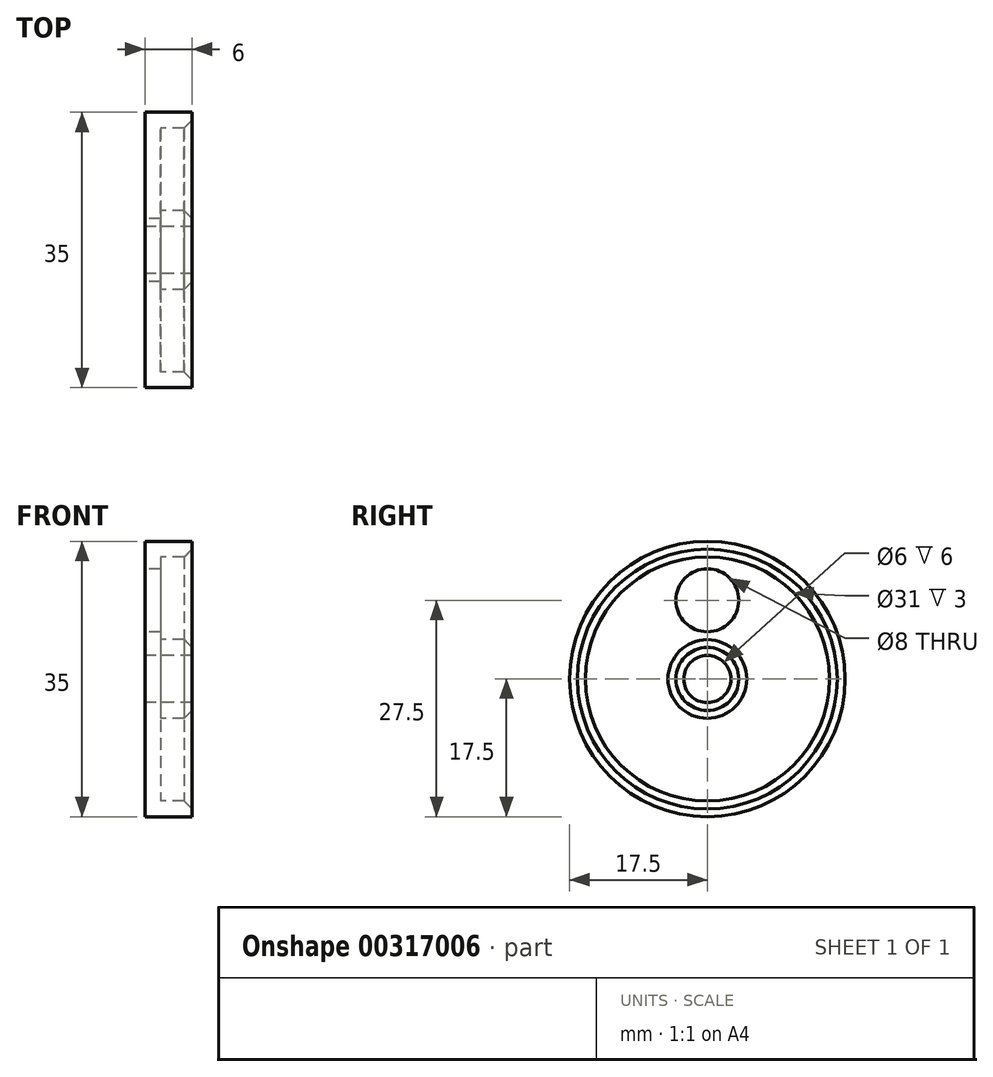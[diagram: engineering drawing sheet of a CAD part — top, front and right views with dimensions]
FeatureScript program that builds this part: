
annotation { "Feature Type Name" : "Feature", "Feature Type Description" : "" }
export const myFeature = defineFeature(function(context is Context, id is Id, definition is map)
    precondition{}
    {
        {
            var Q0;
            Q0=qCreatedBy(makeId("Top.planeOp"),FACE);
            var sketch = newSketch(context, id + "F0", { "sketchPlane" : qUnion([Q0])});
            skLineSegment(sketch, "E0.bottom", {"start": v(0, 0) * mm, "end": v(6, 0) * mm});
            skLineSegment(sketch, "E0.top", {"start": v(0, 17.5) * mm, "end": v(6, 17.5) * mm});
            skLineSegment(sketch, "E0.left", {"start": v(0, 0) * mm, "end": v(0, 17.5) * mm});
            skLineSegment(sketch, "E0.right", {"start": v(6, 0) * mm, "end": v(6, 17.5) * mm});
            skSolve(sketch);
        }
        {
            var Q0;
            Q0 = qSketchRegion(id + "F0", true);
            var Q1;
            Q1=sQuery(id+"F0.wireOp",EDGE,"E0.bottom");
            revolve(context, id + "F1", {"entities" : qUnion([Q0]), "axis" : qUnion([Q1]), "revolveType" : RevolveType.FULL});
        }
        {
            var Q0;
            Q0=qCreatedBy(makeId("Right.planeOp"),FACE);
            var sketch = newSketch(context, id + "F2", { "sketchPlane" : qUnion([Q0])});
            skPoint(sketch, "E1", {"position": v(0, 0) * mm});
            skSolve(sketch);
        }
        {
            var Q0;
            Q0=sQuery(id+"F2.wireOp",VERTEX,"E1");
            var Q1;
            Q1=makeQuery(id+"F1.opRevolve","SWEPT_BODY",BODY,{"disambiguationData":[OSD([sQuery(id+"F0.wireOp",EDGE,"E0.bottom"),sQuery(id+"F0.wireOp",EDGE,"E0.top"),sQuery(id+"F0.wireOp",EDGE,"E0.left"),sQuery(id+"F0.wireOp",EDGE,"E0.right")])]});
            hole(context, id + "F3", {"style" : HoleStyle.SIMPLE, "endStyle" : HoleEndStyle.THROUGH, "oppositeDirection" : true, "holeDiameter" : 6 * mm, "tappedDepth" : 12 * mm, "tapClearance" : 3, "locations" : qUnion([Q0]), "scope" : qUnion([Q1])});
        }
        {
            var Q0;
            Q0=makeQuery(id+"F1.opRevolve","SWEPT_FACE",FACE,{"disambiguationData":[OSD([sQuery(id+"F0.wireOp",EDGE,"E0.right")])]});
            shell(context, id + "F4", {"entities" : qUnion([Q0]), "thickness" : 2 * mm});
        }
        {
            var Q0;
            Q0=qCreatedBy(makeId("Right.planeOp"),FACE);
            var sketch = newSketch(context, id + "F5", { "sketchPlane" : qUnion([Q0])});
            skPoint(sketch, "E2", {"position": v(0, 10) * mm});
            skSolve(sketch);
        }
        {
            var Q0;
            Q0=sQuery(id+"F5.wireOp",VERTEX,"E2");
            var Q1;
            Q1=makeQuery(id+"F1.opRevolve","SWEPT_BODY",BODY,{"disambiguationData":[OSD([sQuery(id+"F0.wireOp",EDGE,"E0.bottom"),sQuery(id+"F0.wireOp",EDGE,"E0.top"),sQuery(id+"F0.wireOp",EDGE,"E0.left"),sQuery(id+"F0.wireOp",EDGE,"E0.right")])]});
            hole(context, id + "F6", {"style" : HoleStyle.SIMPLE, "endStyle" : HoleEndStyle.THROUGH, "oppositeDirection" : true, "holeDiameter" : 8 * mm, "tappedDepth" : 12 * mm, "tapClearance" : 3, "locations" : qUnion([Q0]), "scope" : qUnion([Q1])});
        }
        {
            var Q0;
            Q0=makeQuery(id+"F4.opShell","OFFSET_EDGE",EDGE,{"disambiguationData":[OSD([sQuery(id+"F0.wireOp",EDGE,"E0.right"),sQuery(id+"F3.hole-0.sketch.wireOp",EDGE,"core_line_2")])]});
            chamfer(context, id + "F7", {"entities" : qUnion([Q0]), "width" : 1 * mm, "tangentPropagation" : true});
        }
    });
